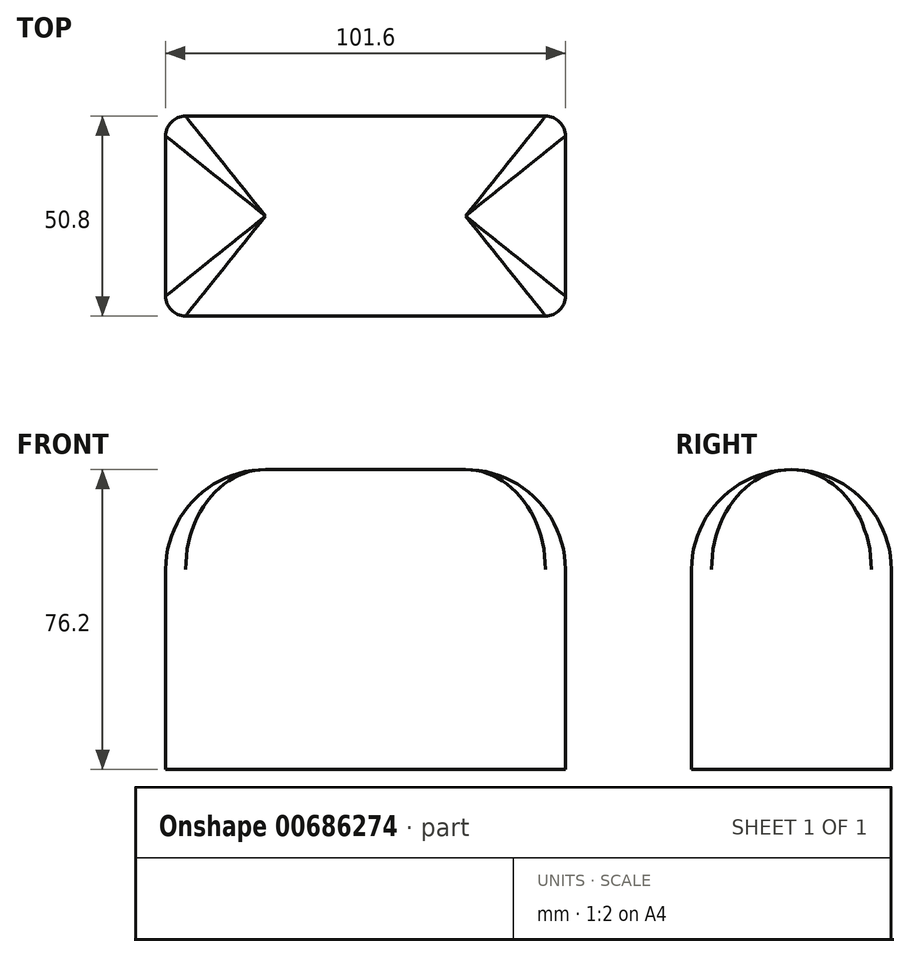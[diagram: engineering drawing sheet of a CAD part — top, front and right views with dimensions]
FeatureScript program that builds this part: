
annotation { "Feature Type Name" : "Feature", "Feature Type Description" : "" }
export const myFeature = defineFeature(function(context is Context, id is Id, definition is map)
    precondition{}
    {
        {
            var Q0;
            Q0=qCreatedBy(makeId("Top.planeOp"),FACE);
            var sketch = newSketch(context, id + "F0", { "sketchPlane" : qUnion([Q0])});
            skLineSegment(sketch, "E0.bottom", {"start": v(50.8, 25.4) * mm, "end": v(-50.8, 25.4) * mm});
            skLineSegment(sketch, "E0.top", {"start": v(50.8, -25.4) * mm, "end": v(-50.8, -25.4) * mm});
            skLineSegment(sketch, "E0.left", {"start": v(50.8, 25.4) * mm, "end": v(50.8, -25.4) * mm});
            skLineSegment(sketch, "E0.right", {"start": v(-50.8, 25.4) * mm, "end": v(-50.8, -25.4) * mm});
            skPoint(sketch, "E0.middle", {"position": v(0, 0) * mm});
            skSolve(sketch);
        }
        {
            var Q0;
            Q0=makeQuery(id+"F0.imprint","IMPRINT",FACE,{"disambiguationData":[TD([[makeQuery(id+"F0.imprint","IMPRINT",EDGE,{"derivedFrom":sQuery(id+"F0.wireOp",EDGE,"E0.bottom")}),1.0]])]});
            extrude(context, id + "F1", {"entities" : qUnion([Q0]), "depth" : 76.2 * mm, "offsetDistance" : 25.4 * mm});
        }
        {
            var Q0;
            Q0=makeQuery(id+"F1.opExtrude","CAP_EDGE",EDGE,{"disambiguationData":[OSD([sQuery(id+"F0.wireOp",EDGE,"E0.right")])],"isStart":false});
            var Q1;
            Q1=makeQuery(id+"F1.opExtrude","CAP_FACE",FACE,{"disambiguationData":[OSD([sQuery(id+"F0.wireOp",EDGE,"E0.bottom"),sQuery(id+"F0.wireOp",EDGE,"E0.top"),sQuery(id+"F0.wireOp",EDGE,"E0.left"),sQuery(id+"F0.wireOp",EDGE,"E0.right")])],"isStart":false});
            fillet(context, id + "F2", {"entities" : qUnion([Q0, Q1]), "radius" : 25.4 * mm, "tangentPropagation" : true, "allowEdgeOverflow" : false});
        }
        {
            var Q0;
            Q0=makeQuery(id+"F2.opFillet","BLEND_EDGE",EDGE,{"blendedFrom":[makeQuery(id+"F1.opExtrude","CAP_EDGE",EDGE,{"disambiguationData":[OSD([sQuery(id+"F0.wireOp",EDGE,"E0.top")])],"isStart":false}),makeQuery(id+"F1.opExtrude","CAP_EDGE",EDGE,{"disambiguationData":[OSD([sQuery(id+"F0.wireOp",EDGE,"E0.left")])],"isStart":false})],"blendedInto":[]});
            var Q1;
            Q1=makeQuery(id+"F2.opFillet","BLEND_EDGE",EDGE,{"blendedFrom":[makeQuery(id+"F1.opExtrude","CAP_EDGE",EDGE,{"disambiguationData":[OSD([sQuery(id+"F0.wireOp",EDGE,"E0.bottom")])],"isStart":false}),makeQuery(id+"F1.opExtrude","CAP_EDGE",EDGE,{"disambiguationData":[OSD([sQuery(id+"F0.wireOp",EDGE,"E0.left")])],"isStart":false})],"blendedInto":[]});
            var Q2;
            Q2=makeQuery(id+"F2.opFillet","BLEND_EDGE",EDGE,{"blendedFrom":[makeQuery(id+"F1.opExtrude","CAP_EDGE",EDGE,{"disambiguationData":[OSD([sQuery(id+"F0.wireOp",EDGE,"E0.top")])],"isStart":false}),makeQuery(id+"F1.opExtrude","CAP_EDGE",EDGE,{"disambiguationData":[OSD([sQuery(id+"F0.wireOp",EDGE,"E0.right")])],"isStart":false})],"blendedInto":[]});
            var Q3;
            Q3=makeQuery(id+"F2.opFillet","BLEND_EDGE",EDGE,{"blendedFrom":[makeQuery(id+"F1.opExtrude","CAP_EDGE",EDGE,{"disambiguationData":[OSD([sQuery(id+"F0.wireOp",EDGE,"E0.bottom")])],"isStart":false}),makeQuery(id+"F1.opExtrude","CAP_EDGE",EDGE,{"disambiguationData":[OSD([sQuery(id+"F0.wireOp",EDGE,"E0.right")])],"isStart":false})],"blendedInto":[]});
            fillet(context, id + "F3", {"entities" : qUnion([Q0, Q1, Q2, Q3]), "radius" : 5.08 * mm, "tangentPropagation" : true, "allowEdgeOverflow" : false});
        }
    });
